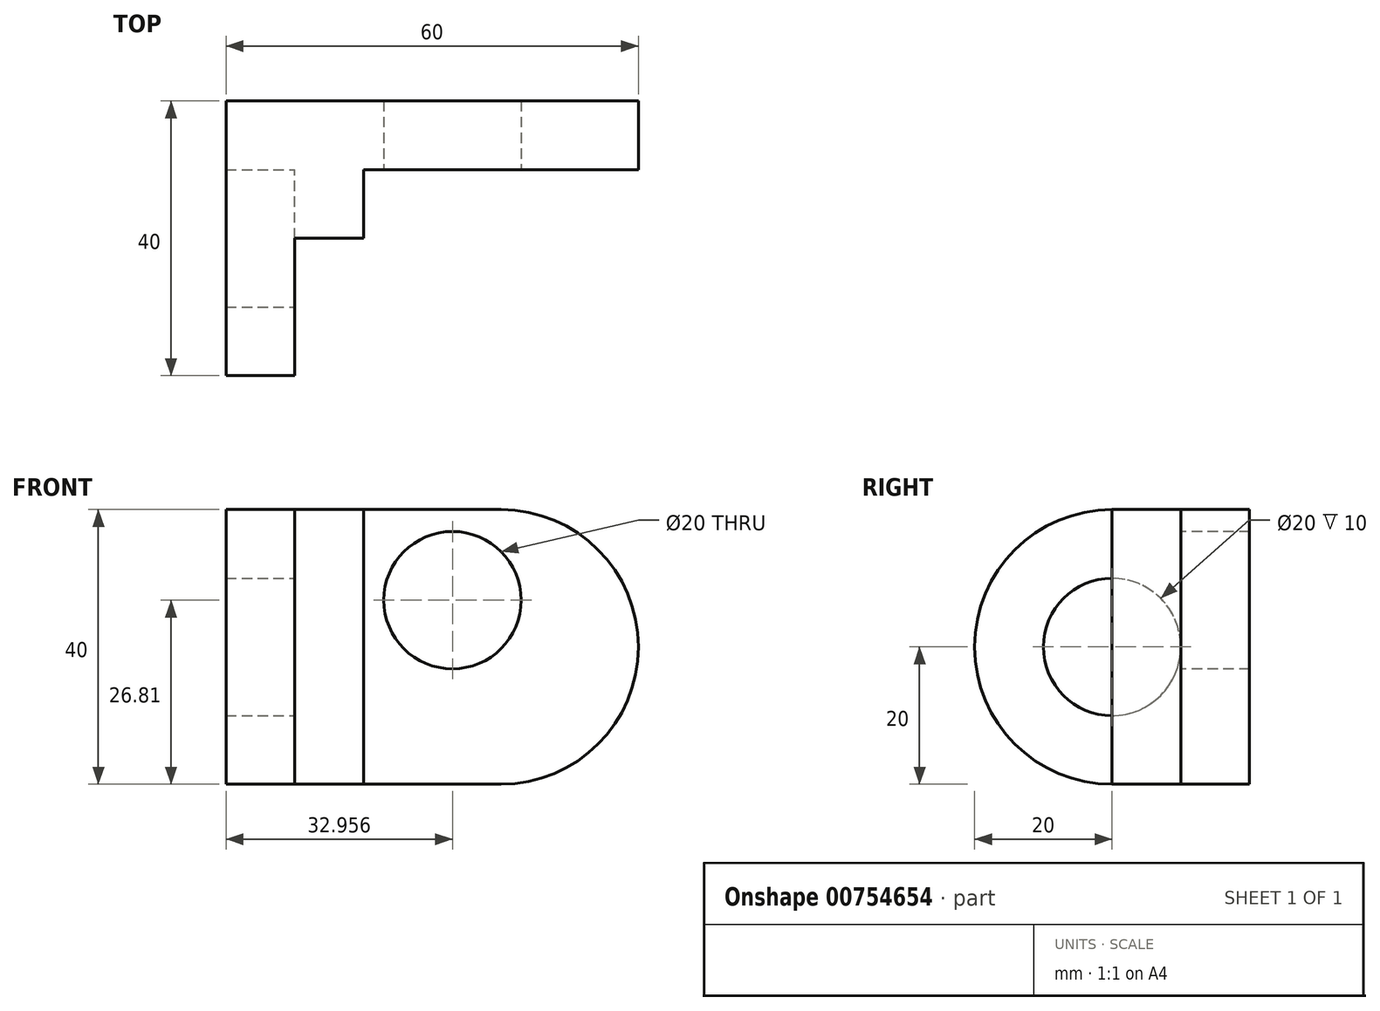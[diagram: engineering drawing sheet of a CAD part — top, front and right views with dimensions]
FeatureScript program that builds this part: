
annotation { "Feature Type Name" : "Feature", "Feature Type Description" : "" }
export const myFeature = defineFeature(function(context is Context, id is Id, definition is map)
    precondition{}
    {
        {
            var Q0;
            Q0=qCreatedBy(makeId("Front.planeOp"),FACE);
            var sketch = newSketch(context, id + "F0", { "sketchPlane" : qUnion([Q0])});
            skLineSegment(sketch, "E0", {"start": v(0, 40) * mm, "end": v(40, 40) * mm});
            skLineSegment(sketch, "E1", {"start": v(40, 40) * mm, "end": v(40, 0) * mm});
            skLineSegment(sketch, "E2", {"start": v(40, 0) * mm, "end": v(0, 0) * mm});
            skLineSegment(sketch, "E3", {"start": v(0, 0) * mm, "end": v(0, 40) * mm});
            skArc(sketch, "E4", {"start": v(40, 0) * mm, "mid": v(60, 20) * mm, "end": v(40, 40) * mm});
            skSolve(sketch);
        }
        {
            var Q0;
            Q0 = qSketchRegion(id + "F0", true);
            extrude(context, id + "F1", {"entities" : qUnion([Q0]), "depth" : 10 * mm, "offsetDistance" : 25 * mm});
        }
        {
            var Q0;
            Q0=makeQuery(id+"F1.opExtrude","CAP_FACE",FACE,{"disambiguationData":[OSD([sQuery(id+"F0.wireOp",EDGE,"E0"),sQuery(id+"F0.wireOp",EDGE,"E2"),sQuery(id+"F0.wireOp",EDGE,"E3"),sQuery(id+"F0.wireOp",EDGE,"E4")])],"isStart":false});
            var sketch = newSketch(context, id + "F2", { "sketchPlane" : qUnion([Q0])});
            skLineSegment(sketch, "E5", {"start": v(0, 0) * mm, "end": v(40, 0) * mm});
            skLineSegment(sketch, "E6", {"start": v(40, 0) * mm, "end": v(30, 0) * mm});
            skLineSegment(sketch, "E7", {"start": v(30, 0) * mm, "end": v(20, 0) * mm});
            skLineSegment(sketch, "E8", {"start": v(20, 0) * mm, "end": v(10, 0) * mm});
            skLineSegment(sketch, "E9", {"start": v(10, 0) * mm, "end": v(0, 0) * mm});
            skLineSegment(sketch, "E10", {"start": v(10, 0) * mm, "end": v(10, 40) * mm});
            skLineSegment(sketch, "E11", {"start": v(10, 40) * mm, "end": v(0, 40) * mm});
            skLineSegment(sketch, "E12", {"start": v(0, 40) * mm, "end": v(0, 0) * mm});
            skLineSegment(sketch, "E13", {"start": v(10, 0) * mm, "end": v(20, 0) * mm});
            skLineSegment(sketch, "E14", {"start": v(20, 0) * mm, "end": v(20, 40) * mm});
            skLineSegment(sketch, "E15", {"start": v(20, 40) * mm, "end": v(10, 40) * mm});
            skSolve(sketch);
        }
        {
            var Q0;
            Q0=makeQuery(id+"F2.imprint","IMPRINT",FACE,{"disambiguationData":[TD([[makeQuery(id+"F2.imprint","IMPRINT",EDGE,{"derivedFrom":sQuery(id+"F2.wireOp",EDGE,"E10")}),-1.0]])]});
            extrude(context, id + "F3", {"entities" : qUnion([Q0]), "operationType" : NewBodyOperationType.ADD, "depth" : 10 * mm, "offsetDistance" : 25 * mm});
        }
        {
            var Q0;
            {var subQ0=sQuery(id+"F0.wireOp",EDGE,"E3");var subQ1=sQuery(id+"F0.wireOp",EDGE,"E2");var subQ2=sQuery(id+"F0.wireOp",EDGE,"E0");Q0=makeQuery(id+"F3.boolean.opBoolean","SPLIT",FACE,{"disambiguationData":[TD([makeQuery(id+"F1.opExtrude","SWEPT_FACE",FACE,{"disambiguationData":[OSD([subQ0])]})])],"derivedFrom":makeQuery(id+"F1.opExtrude","CAP_FACE",FACE,{"disambiguationData":[OSD([subQ2,subQ1,subQ0,sQuery(id+"F0.wireOp",EDGE,"E4")])],"isStart":false})});}
            extrude(context, id + "F4", {"entities" : qUnion([Q0]), "operationType" : NewBodyOperationType.ADD, "depth" : 30 * mm, "offsetDistance" : 25 * mm});
        }
        {
            var Q0;
            {var subQ0=sQuery(id+"F0.wireOp",EDGE,"E2");var subQ1=sQuery(id+"F0.wireOp",EDGE,"E4");var subQ2=sQuery(id+"F0.wireOp",EDGE,"E0");Q0=makeQuery(id+"F3.boolean.opBoolean","SPLIT",FACE,{"disambiguationData":[TD([makeQuery(id+"F1.opExtrude","SWEPT_FACE",FACE,{"disambiguationData":[OSD([subQ1])]})])],"derivedFrom":makeQuery(id+"F1.opExtrude","CAP_FACE",FACE,{"disambiguationData":[OSD([subQ2,subQ0,sQuery(id+"F0.wireOp",EDGE,"E3"),subQ1])],"isStart":false})});}
            var sketch = newSketch(context, id + "F5", { "sketchPlane" : qUnion([Q0])});
            skCircle(sketch, "E16", {"center": v(32.96, 26.8) * mm, "radius": 10 * mm});
            skSolve(sketch);
        }
        {
            var Q0;
            Q0 = qSketchRegion(id + "F5", true);
            extrude(context, id + "F6", {"entities" : qUnion([Q0]), "operationType" : NewBodyOperationType.REMOVE, "oppositeDirection" : true, "depth" : 10 * mm, "offsetDistance" : 25 * mm});
        }
        {
            var Q0;
            Q0=makeQuery(id+"F4.opExtrude","SWEPT_FACE",FACE,{"disambiguationData":[OSD([sQuery(id+"F2.wireOp",EDGE,"E10")])]});
            var sketch = newSketch(context, id + "F7", { "sketchPlane" : qUnion([Q0])});
            skCircle(sketch, "E17", {"center": v(-20, 20) * mm, "radius": 10 * mm});
            skSolve(sketch);
        }
        {
            var Q0;
            Q0 = qSketchRegion(id + "F7", true);
            extrude(context, id + "F8", {"entities" : qUnion([Q0]), "operationType" : NewBodyOperationType.REMOVE, "oppositeDirection" : true, "depth" : 16.7 * mm, "offsetDistance" : 25 * mm});
        }
        {
            var Q0;
            Q0=makeQuery(id+"F3.opExtrude","SWEPT_FACE",FACE,{"disambiguationData":[OSD([sQuery(id+"F2.wireOp",EDGE,"E14")])]});
            var sketch = newSketch(context, id + "F9", { "sketchPlane" : qUnion([Q0])});
            skCircle(sketch, "E18", {"center": v(-20, 20) * mm, "radius": 10 * mm});
            skSolve(sketch);
        }
        {
            var Q0;
            {var subQ0=sQuery(id+"F9.wireOp",EDGE,"E18");var subQ1=sQuery(id+"F2.wireOp",EDGE,"E14");var subQ2=makeQuery(id+"F3.opExtrude","CAP_EDGE",EDGE,{"disambiguationData":[OSD([subQ1])],"isStart":false});var subQ3=makeQuery(id+"F9.imprint","INTERSECT",VERTEX,{"disambiguationData":[OD(0.0)],"derivedFrom":[subQ2,subQ0]});Q0=makeQuery(id+"F9.imprint","IMPRINT",FACE,{"disambiguationData":[TD([[makeQuery(id+"F9.imprint","IMPRINT",EDGE,{"disambiguationData":[TD([[subQ3,1.0]])],"derivedFrom":subQ0}),1.0]])]});}
            extrude(context, id + "F10", {"entities" : qUnion([Q0]), "operationType" : NewBodyOperationType.REMOVE, "oppositeDirection" : true, "depth" : 25 * mm, "offsetDistance" : 25 * mm});
        }
        {
            var Q0;
            Q0=makeQuery(id+"F4.opExtrude","SWEPT_FACE",FACE,{"disambiguationData":[OSD([sQuery(id+"F2.wireOp",EDGE,"E10")])]});
            var sketch = newSketch(context, id + "F11", { "sketchPlane" : qUnion([Q0])});
            skArc(sketch, "E19", {"start": v(-20, 40) * mm, "mid": v(-40, 20) * mm, "end": v(-20, 0) * mm});
            skSolve(sketch);
        }
        {
            var Q0;
            {var subQ1=sQuery(id+"F2.wireOp",EDGE,"E10");var subQ3=sQuery(id+"F2.wireOp",EDGE,"E15");var subQ7=makeQuery(id+"F4.opExtrude","SWEPT_EDGE",EDGE,{"disambiguationData":[OSD([subQ1,sQuery(id+"F2.wireOp",EDGE,"E11"),subQ3])]});Q0=makeQuery(id+"F11.imprint","IMPRINT",FACE,{"disambiguationData":[TD([[makeQuery(id+"F11.imprint","IMPRINT",EDGE,{"derivedFrom":subQ7}),-1.0]])]});}
            extrude(context, id + "F12", {"entities" : qUnion([Q0]), "operationType" : NewBodyOperationType.REMOVE, "oppositeDirection" : true, "depth" : 25 * mm, "offsetDistance" : 25 * mm});
        }
        {
            var Q0;
            Q0=makeQuery(id+"F4.opExtrude","SWEPT_FACE",FACE,{"disambiguationData":[OSD([sQuery(id+"F2.wireOp",EDGE,"E10")])]});
            var sketch = newSketch(context, id + "F13", { "sketchPlane" : qUnion([Q0])});
            skArc(sketch, "E20", {"start": v(-40, 20) * mm, "mid": v(-34.14, 5.86) * mm, "end": v(-20, 0) * mm});
            skSolve(sketch);
        }
        {
            var Q0;
            Q0=makeQuery(id+"F13.imprint","IMPRINT",FACE,{"disambiguationData":[TD([[makeQuery(id+"F13.imprint","IMPRINT",EDGE,{"derivedFrom":sQuery(id+"F13.wireOp",EDGE,"E20")}),-1.0]])]});
            extrude(context, id + "F14", {"entities" : qUnion([Q0]), "operationType" : NewBodyOperationType.REMOVE, "oppositeDirection" : true, "depth" : 25 * mm, "offsetDistance" : 25 * mm});
        }
    });
